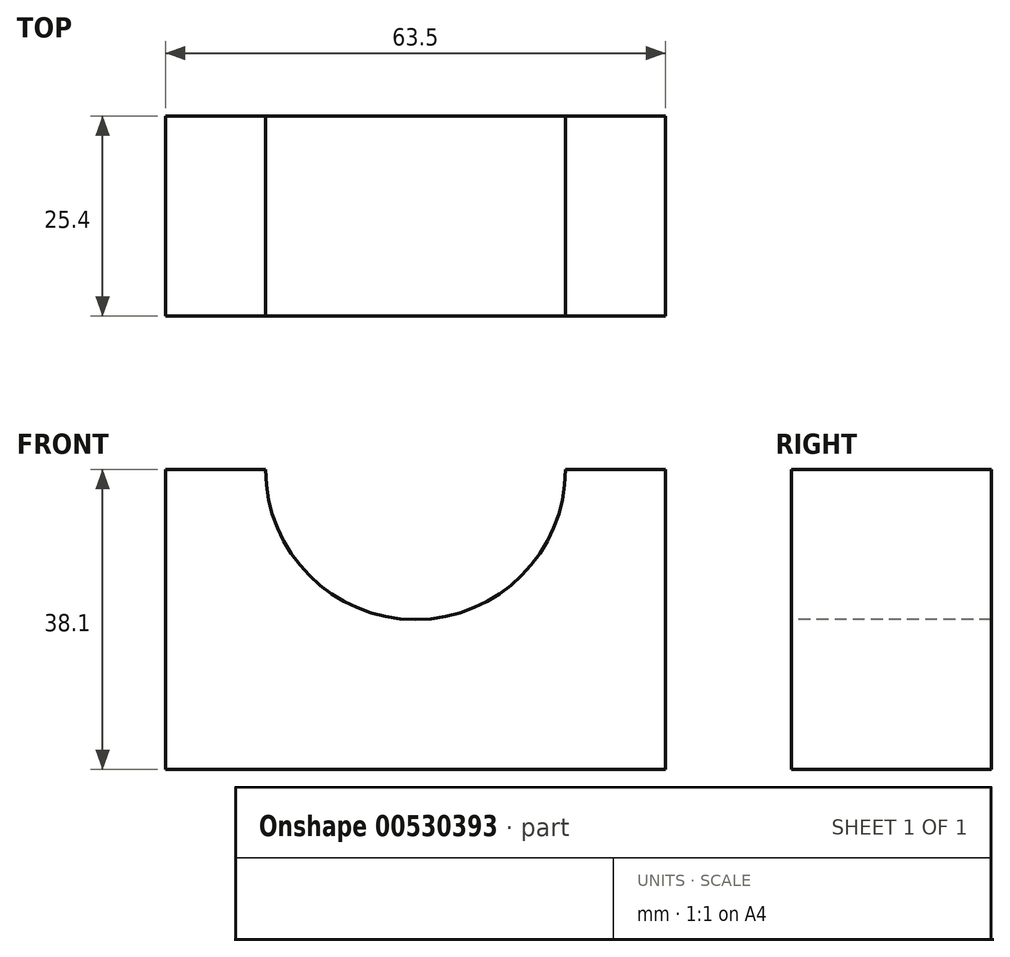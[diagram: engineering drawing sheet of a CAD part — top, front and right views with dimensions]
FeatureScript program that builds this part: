
annotation { "Feature Type Name" : "Feature", "Feature Type Description" : "" }
export const myFeature = defineFeature(function(context is Context, id is Id, definition is map)
    precondition{}
    {
        {
            var Q0;
            Q0=qCreatedBy(makeId("Front.planeOp"),FACE);
            var sketch = newSketch(context, id + "F0", { "sketchPlane" : qUnion([Q0])});
            skLineSegment(sketch, "E0.bottom", {"start": v(-20.2, 42.05) * mm, "end": v(43.3, 42.05) * mm});
            skLineSegment(sketch, "E0.top", {"start": v(-20.2, 3.95) * mm, "end": v(43.3, 3.95) * mm});
            skLineSegment(sketch, "E0.left", {"start": v(-20.2, 42.05) * mm, "end": v(-20.2, 3.95) * mm});
            skLineSegment(sketch, "E0.right", {"start": v(43.3, 42.05) * mm, "end": v(43.3, 3.95) * mm});
            skSolve(sketch);
        }
        {
            var Q0;
            Q0=makeQuery(id+"F0.imprint","IMPRINT",FACE,{"disambiguationData":[TD([[makeQuery(id+"F0.imprint","IMPRINT",EDGE,{"derivedFrom":sQuery(id+"F0.wireOp",EDGE,"E0.bottom")}),-1.0]])]});
            extrude(context, id + "F1", {"entities" : qUnion([Q0]), "depth" : 25.4 * mm, "offsetDistance" : 25.4 * mm});
        }
        {
            var Q0;
            Q0=makeQuery(id+"F1.opExtrude","CAP_FACE",FACE,{"disambiguationData":[OSD([sQuery(id+"F0.wireOp",EDGE,"E0.bottom"),sQuery(id+"F0.wireOp",EDGE,"E0.top"),sQuery(id+"F0.wireOp",EDGE,"E0.left"),sQuery(id+"F0.wireOp",EDGE,"E0.right")])],"isStart":false});
            var sketch = newSketch(context, id + "F2", { "sketchPlane" : qUnion([Q0])});
            skArc(sketch, "E1", {"start": v(-7.5, 42.05) * mm, "mid": v(11.56, 23) * mm, "end": v(30.6, 42.05) * mm});
            skSolve(sketch);
        }
        {
            var Q0;
            {var subQ0=sQuery(id+"F2.wireOp",EDGE,"E1");Q0=makeQuery(id+"F2.imprint","IMPRINT",FACE,{"disambiguationData":[TD([[makeQuery(id+"F2.imprint","IMPRINT",EDGE,{"derivedFrom":subQ0}),1.0]])]});}
            extrude(context, id + "F3", {"entities" : qUnion([Q0]), "operationType" : NewBodyOperationType.REMOVE, "endBound" : BoundingType.THROUGH_ALL, "oppositeDirection" : true, "depth" : 25.4 * mm, "offsetDistance" : 25.4 * mm});
        }
    });
